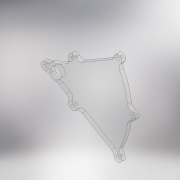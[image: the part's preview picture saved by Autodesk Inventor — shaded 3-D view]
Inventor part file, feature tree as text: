
AUTODESK INVENTOR PART (.ipt)
format: ipt  version: 2018.2 (Build 222227000, 227)  size: 200,704 bytes
history: native  units: mm
features: extrude x2, sketch x1, fillet x1
ambient origin geometry x8: Origin, YZ Plane, XZ Plane, XY Plane, X Axis, Y Axis, Z Axis, Center Point
bodies: Solid1 (feature_tree)
feature tree (4):
  sketch  "Sketch1"  dims[d0=16.0mm d1=101.0mm d3=12.0mm d4=6.0mm d5=0.0mm d6=60.0deg d7=2.0mm d8=5.0mm d9=3.0mm d10=4.0mm d12=5.0mm d13=5.0mm d14=5.0mm d15=5.0mm d16=5.0mm d17=5.0mm d18=25.0mm d19=6.0mm d20=6.0mm d21=6.0mm d22=0.0mm d23=8.0mm]
  extrude  "Extrusion1"  Depth=8.0mm
  extrude  "Extrusion2"  Depth=12.0mm
  fillet  "Fillet1"  Radius=6.0mm
